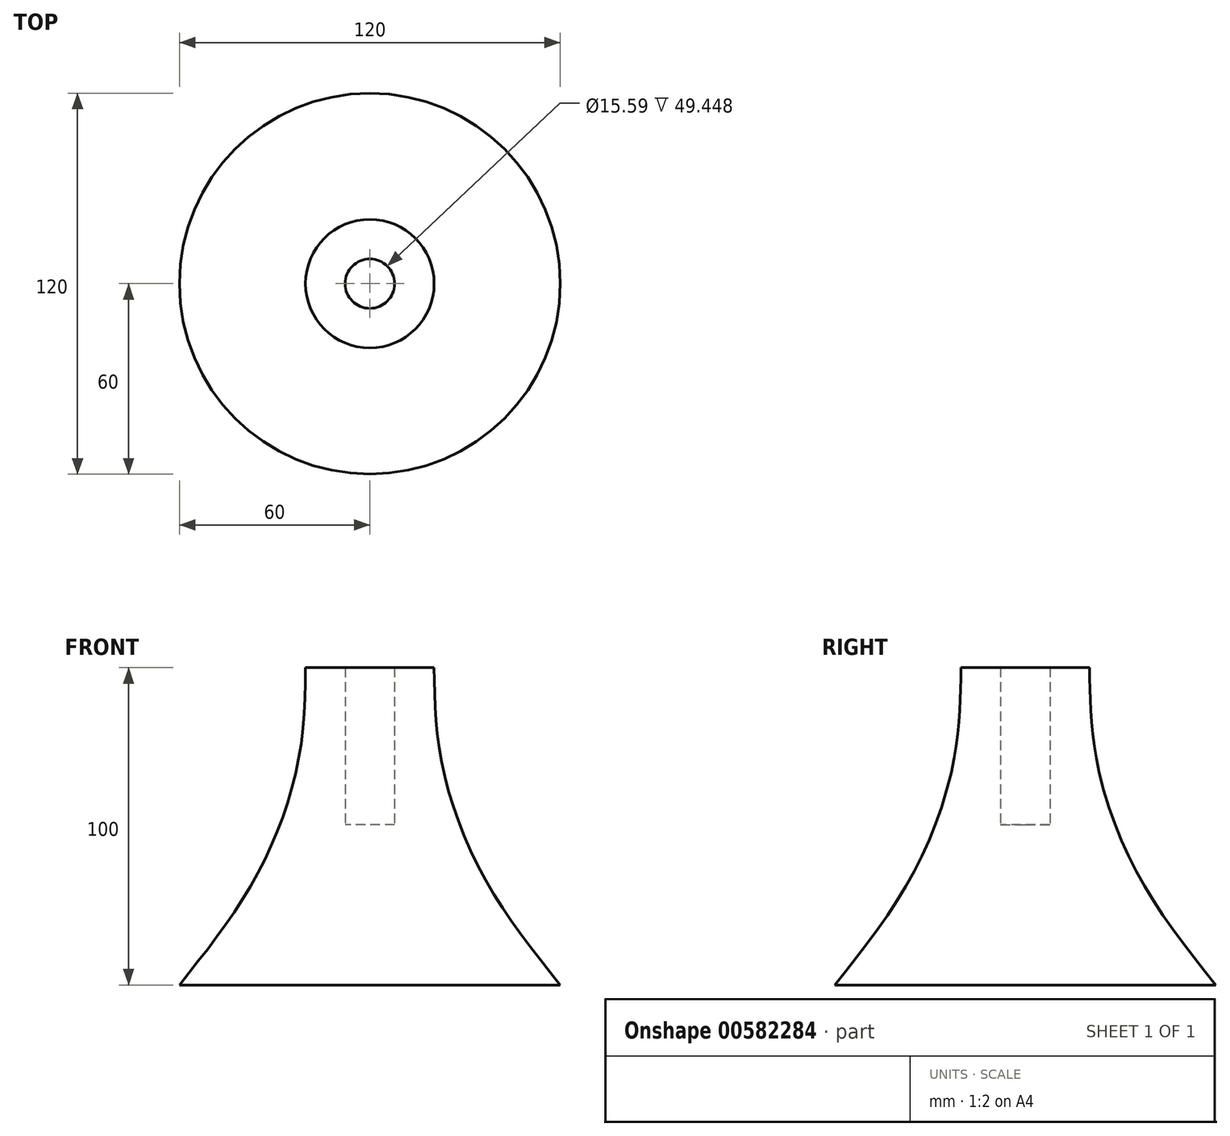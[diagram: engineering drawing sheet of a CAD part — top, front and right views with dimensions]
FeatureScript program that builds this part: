
annotation { "Feature Type Name" : "Feature", "Feature Type Description" : "" }
export const myFeature = defineFeature(function(context is Context, id is Id, definition is map)
    precondition{}
    {
        {
            var Q0;
            Q0=qCreatedBy(makeId("Front.planeOp"),FACE);
            var sketch = newSketch(context, id + "F0", { "sketchPlane" : qUnion([Q0])});
            skLineSegment(sketch, "E0", {"start": v(0, 49.45) * mm, "end": v(0, -50.55) * mm});
            skLineSegment(sketch, "E1", {"start": v(0, -50.55) * mm, "end": v(60, -50.55) * mm});
            skLineSegment(sketch, "E2", {"start": v(0, 49.45) * mm, "end": v(20.25, 49.45) * mm});
            skFitSpline(sketch, "E3", {"points": [v(20.25, 49.45) * mm, v(22.45, 20.53) * mm, v(36.02, -16.68) * mm, v(60, -50.55) * mm], "startDerivative": vector(1.32, -94.15) * mm, "endDerivative": vector(72.84, -91.34) * mm});
            skSolve(sketch);
        }
        {
            var Q0;
            Q0=makeQuery(id+"F0.imprint","IMPRINT",FACE,{"disambiguationData":[TD([[makeQuery(id+"F0.imprint","IMPRINT",EDGE,{"derivedFrom":sQuery(id+"F0.wireOp",EDGE,"E0")}),1.0]])]});
            var Q1;
            Q1=sQuery(id+"F0.wireOp",EDGE,"E0");
            revolve(context, id + "F1", {"entities" : qUnion([Q0]), "axis" : qUnion([Q1]), "revolveType" : RevolveType.FULL});
        }
        {
            var Q0;
            Q0=qCreatedBy(makeId("Top.planeOp"),FACE);
            var sketch = newSketch(context, id + "F2", { "sketchPlane" : qUnion([Q0])});
            skCircle(sketch, "E4", {"center": v(0, 0) * mm, "radius": 7.8 * mm});
            skSolve(sketch);
        }
        {
            var Q0;
            Q0 = qSketchRegion(id + "F2", true);
            extrude(context, id + "F3", {"entities" : qUnion([Q0]), "operationType" : NewBodyOperationType.REMOVE, "depth" : 100 * mm, "offsetDistance" : 25 * mm});
        }
    });
